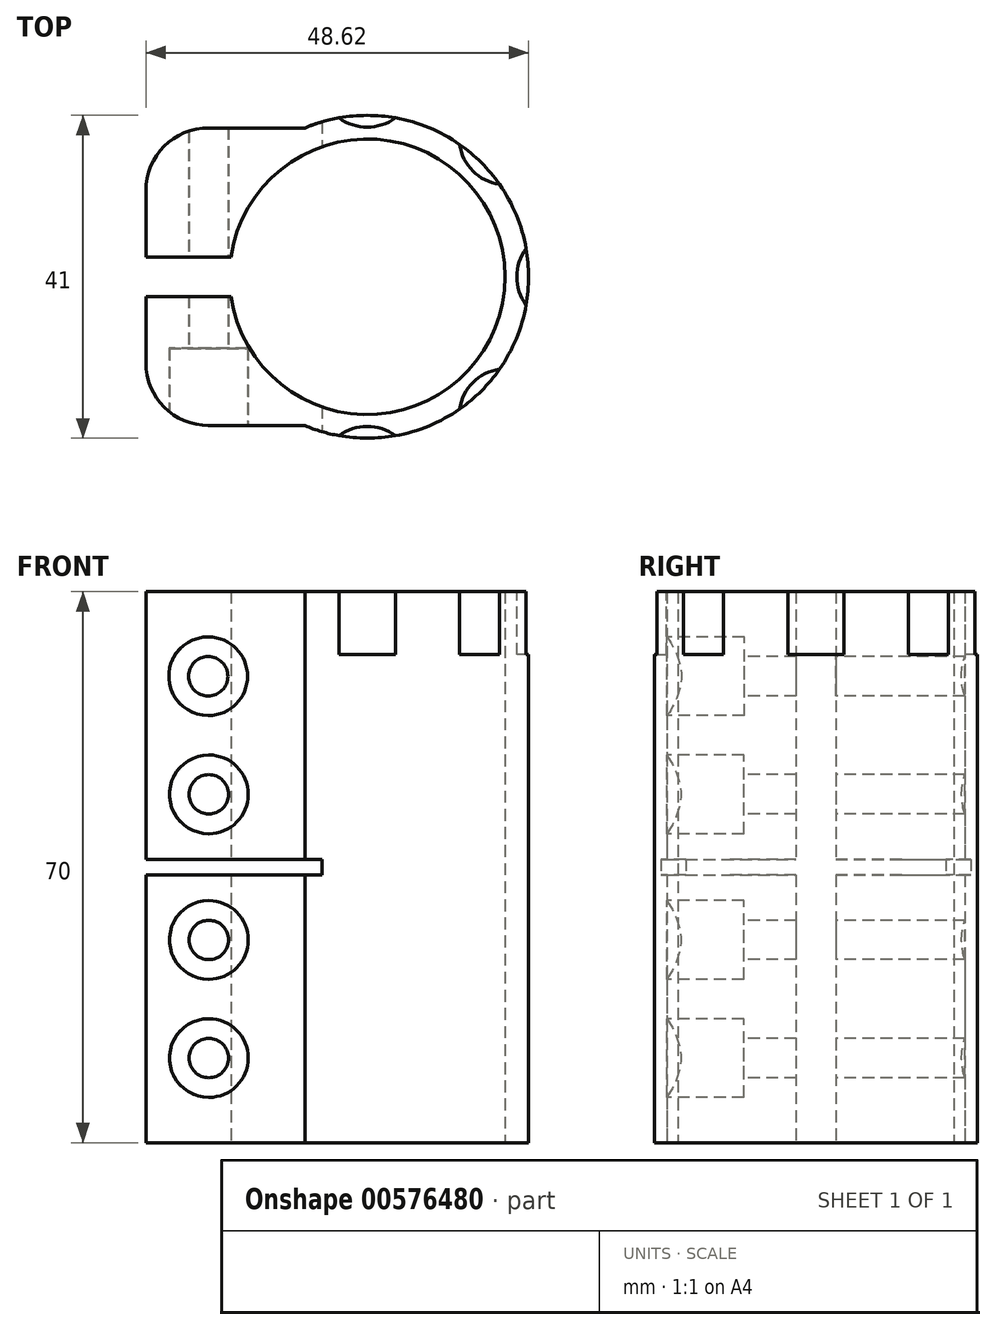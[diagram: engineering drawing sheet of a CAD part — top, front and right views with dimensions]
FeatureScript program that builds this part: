
annotation { "Feature Type Name" : "Feature", "Feature Type Description" : "" }
export const myFeature = defineFeature(function(context is Context, id is Id, definition is map)
    precondition{}
    {
        {
            var Q0;
            Q0=qCreatedBy(makeId("Top.planeOp"),FACE);
            var sketch = newSketch(context, id + "F0", { "sketchPlane" : qUnion([Q0])});
            skArc(sketch, "E0", {"start": v(-17.32, -2.5) * mm, "mid": v(17.5, 0) * mm, "end": v(-17.32, 2.5) * mm});
            skLineSegment(sketch, "E1", {"start": v(-7.92, 18.9) * mm, "end": v(-20.12, 18.9) * mm});
            skLineSegment(sketch, "E2", {"start": v(-28.12, 10.9) * mm, "end": v(-28.12, 2.5) * mm});
            skLineSegment(sketch, "E3", {"start": v(-28.12, 2.5) * mm, "end": v(-17.32, 2.5) * mm});
            skPoint(sketch, "E4.visualSharp", {"position": v(-28.12, 18.9) * mm});
            skArc(sketch, "E4.filletArc", {"start": v(-20.12, 18.9) * mm, "mid": v(-25.78, 16.57) * mm, "end": v(-28.12, 10.9) * mm});
            skLineSegment(sketch, "E5", {"start": v(0, 0) * mm, "end": v(34.56, 0) * mm, "construction": true});
            skLineSegment(sketch, "E6.MirrorCS", {"start": v(-28.12, -2.5) * mm, "end": v(-17.32, -2.5) * mm});
            skLineSegment(sketch, "E7.MirrorCS", {"start": v(-7.92, -18.9) * mm, "end": v(-20.12, -18.9) * mm});
            skLineSegment(sketch, "E8.MirrorCS", {"start": v(-28.12, -10.9) * mm, "end": v(-28.12, -2.5) * mm});
            skArc(sketch, "E9.MirrorCS", {"start": v(-20.12, -18.9) * mm, "mid": v(-25.78, -16.57) * mm, "end": v(-28.12, -10.9) * mm});
            skArc(sketch, "E10.trimOffspring", {"start": v(-7.92, -18.9) * mm, "mid": v(20.5, 0) * mm, "end": v(-7.92, 18.9) * mm});
            skSolve(sketch);
        }
        {
            var Q0;
            Q0=makeQuery(id+"F0.imprint","IMPRINT",FACE,{"disambiguationData":[TD([[makeQuery(id+"F0.imprint","IMPRINT",EDGE,{"derivedFrom":sQuery(id+"F0.wireOp",EDGE,"E0")}),-1.0]])]});
            extrude(context, id + "F1", {"entities" : qUnion([Q0]), "endBound" : BoundingType.SYMMETRIC, "depth" : 70 * mm, "offsetDistance" : 25 * mm});
        }
        {
            var Q0;
            Q0=makeQuery(id+"F1.opExtrude","SWEPT_FACE",FACE,{"disambiguationData":[OSD([sQuery(id+"F0.wireOp",EDGE,"E7.MirrorCS")])]});
            var sketch = newSketch(context, id + "F2", { "sketchPlane" : qUnion([Q0])});
            skPoint(sketch, "E11", {"position": v(-20.12, -24.25) * mm});
            skPoint(sketch, "E12", {"position": v(-20.12, -9.25) * mm});
            skPoint(sketch, "E13", {"position": v(-20.12, 9.25) * mm});
            skPoint(sketch, "E14", {"position": v(-20.2, 24.25) * mm});
            skSolve(sketch);
        }
        {
            var Q0;
            Q0=sQuery(id+"F2.wireOp",VERTEX,"E11");
            var Q1;
            Q1=sQuery(id+"F2.wireOp",VERTEX,"E12");
            var Q2;
            Q2=sQuery(id+"F2.wireOp",VERTEX,"E13");
            var Q3;
            Q3=sQuery(id+"F2.wireOp",VERTEX,"E14");
            var Q4;
            Q4=makeQuery(id+"F1.opExtrude","SWEPT_BODY",BODY,{"disambiguationData":[OSD([sQuery(id+"F0.wireOp",EDGE,"E0"),sQuery(id+"F0.wireOp",EDGE,"E1"),sQuery(id+"F0.wireOp",EDGE,"E2"),sQuery(id+"F0.wireOp",EDGE,"E3"),sQuery(id+"F0.wireOp",EDGE,"E4.filletArc"),sQuery(id+"F0.wireOp",EDGE,"E6.MirrorCS"),sQuery(id+"F0.wireOp",EDGE,"E7.MirrorCS"),sQuery(id+"F0.wireOp",EDGE,"E8.MirrorCS"),sQuery(id+"F0.wireOp",EDGE,"E9.MirrorCS"),sQuery(id+"F0.wireOp",EDGE,"E10.trimOffspring")])]});
            hole(context, id + "F3", {"style" : HoleStyle.C_BORE, "endStyle" : HoleEndStyle.THROUGH, "holeDiameter" : 5 * mm, "cBoreDiameter" : 10 * mm, "cBoreDepth" : 8 * mm, "majorDiameter" : 5 * mm, "isTappedThrough" : true, "tappedDepth" : 12 * mm, "tapClearance" : 3, "locations" : qUnion([Q0, Q1, Q2, Q3]), "scope" : qUnion([Q4])});
        }
        {
            var Q0;
            Q0=qCreatedBy(makeId("Front.planeOp"),FACE);
            var sketch = newSketch(context, id + "F4", { "sketchPlane" : qUnion([Q0])});
            skLineSegment(sketch, "E15.bottom", {"start": v(-28.12, 1) * mm, "end": v(-5.72, 1) * mm});
            skLineSegment(sketch, "E15.top", {"start": v(-28.12, -1) * mm, "end": v(-5.72, -1) * mm});
            skLineSegment(sketch, "E15.left", {"start": v(-28.12, 1) * mm, "end": v(-28.12, -1) * mm});
            skLineSegment(sketch, "E15.right", {"start": v(-5.72, 1) * mm, "end": v(-5.72, -1) * mm});
            skSolve(sketch);
        }
        {
            var Q0;
            Q0 = qSketchRegion(id + "F4", true);
            extrude(context, id + "F5", {"entities" : qUnion([Q0]), "operationType" : NewBodyOperationType.REMOVE, "endBound" : BoundingType.SYMMETRIC, "oppositeDirection" : true, "depth" : 50 * mm, "offsetDistance" : 25 * mm});
        }
        {
            var Q0;
            Q0=makeQuery(id+"F1.opExtrude","CAP_FACE",FACE,{"disambiguationData":[OSD([sQuery(id+"F0.wireOp",EDGE,"E0"),sQuery(id+"F0.wireOp",EDGE,"E1"),sQuery(id+"F0.wireOp",EDGE,"E2"),sQuery(id+"F0.wireOp",EDGE,"E3"),sQuery(id+"F0.wireOp",EDGE,"E4.filletArc"),sQuery(id+"F0.wireOp",EDGE,"E6.MirrorCS"),sQuery(id+"F0.wireOp",EDGE,"E7.MirrorCS"),sQuery(id+"F0.wireOp",EDGE,"E8.MirrorCS"),sQuery(id+"F0.wireOp",EDGE,"E9.MirrorCS"),sQuery(id+"F0.wireOp",EDGE,"E10.trimOffspring")])],"isStart":false});
            var sketch = newSketch(context, id + "F6", { "sketchPlane" : qUnion([Q0])});
            skCircle(sketch, "E16", {"center": v(0, -25) * mm, "radius": 6 * mm});
            skCircle(sketch, "E17.1.0", {"center": v(17.68, -17.68) * mm, "radius": 6 * mm});
            skCircle(sketch, "E17.2.0", {"center": v(25, 0) * mm, "radius": 6 * mm});
            skCircle(sketch, "E17.3.0", {"center": v(17.68, 17.68) * mm, "radius": 6 * mm});
            skCircle(sketch, "E17.4.0", {"center": v(0, 25) * mm, "radius": 6 * mm});
            skPoint(sketch, "E17.center", {"position": v(0, 0) * mm});
            skLineSegment(sketch, "E17.anchor1", {"start": v(0, 0) * mm, "end": v(0, -25) * mm, "construction": true});
            skLineSegment(sketch, "E17.anchor2", {"start": v(0, 0) * mm, "end": v(0, 25) * mm, "construction": true});
            skSolve(sketch);
        }
        {
            var Q0;
            Q0 = qSketchRegion(id + "F6", true);
            extrude(context, id + "F7", {"entities" : qUnion([Q0]), "operationType" : NewBodyOperationType.REMOVE, "oppositeDirection" : true, "depth" : 8 * mm, "offsetDistance" : 25 * mm});
        }
    });
